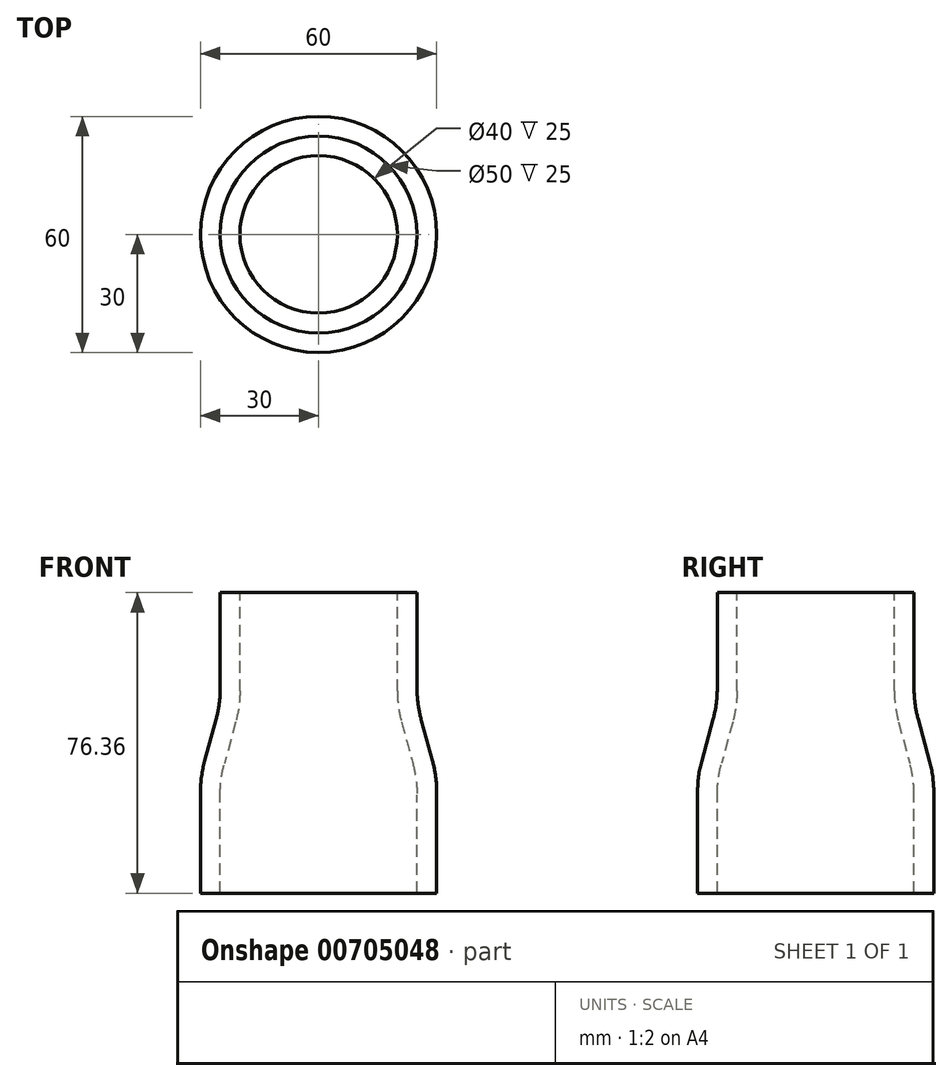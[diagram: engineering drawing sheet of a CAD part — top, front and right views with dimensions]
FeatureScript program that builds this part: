
annotation { "Feature Type Name" : "Feature", "Feature Type Description" : "" }
export const myFeature = defineFeature(function(context is Context, id is Id, definition is map)
    precondition{}
    {
        {
            var Q0;
            Q0=qCreatedBy(makeId("Front.planeOp"),FACE);
            var sketch = newSketch(context, id + "F0", { "sketchPlane" : qUnion([Q0])});
            skLineSegment(sketch, "E0", {"start": v(0, 61.45) * mm, "end": v(0, -56.79) * mm, "construction": true});
            skLineSegment(sketch, "E1", {"start": v(-25, 0) * mm, "end": v(-25, 25) * mm});
            skLineSegment(sketch, "E2", {"start": v(-23.94, 32.9) * mm, "end": v(-21.06, 43.46) * mm});
            skLineSegment(sketch, "E3", {"start": v(-20, 51.36) * mm, "end": v(-20, 76.36) * mm});
            skLineSegment(sketch, "E4.0", {"start": v(-25, 52.03) * mm, "end": v(-25, 76.36) * mm});
            skLineSegment(sketch, "E4.1", {"start": v(-28.94, 33.57) * mm, "end": v(-26.06, 44.13) * mm});
            skLineSegment(sketch, "E4.2", {"start": v(-30, 0) * mm, "end": v(-30, 25.67) * mm});
            skLineSegment(sketch, "E5", {"start": v(-25, 76.36) * mm, "end": v(-20, 76.36) * mm});
            skLineSegment(sketch, "E6", {"start": v(-30, 0) * mm, "end": v(-25, 0) * mm});
            skPoint(sketch, "E7.visualSharp", {"position": v(-25, 29.02) * mm});
            skArc(sketch, "E7.filletArc", {"start": v(-23.94, 32.9) * mm, "mid": v(-24.73, 28.99) * mm, "end": v(-25, 25) * mm});
            skPoint(sketch, "E8.visualSharp", {"position": v(-30, 29.7) * mm});
            skArc(sketch, "E8.filletArc", {"start": v(-28.94, 33.57) * mm, "mid": v(-29.73, 29.66) * mm, "end": v(-30, 25.67) * mm});
            skPoint(sketch, "E9.visualSharp", {"position": v(-20, 47.34) * mm});
            skArc(sketch, "E9.filletArc", {"start": v(-21.06, 43.46) * mm, "mid": v(-20.27, 47.37) * mm, "end": v(-20, 51.36) * mm});
            skPoint(sketch, "E10.visualSharp", {"position": v(-25, 48) * mm});
            skArc(sketch, "E10.filletArc", {"start": v(-26.06, 44.13) * mm, "mid": v(-25.27, 48.04) * mm, "end": v(-25, 52.03) * mm});
            skSolve(sketch);
        }
        {
            var Q0;
            Q0 = qSketchRegion(id + "F0", true);
            var Q1;
            Q1=sQuery(id+"F0.wireOp",EDGE,"E0");
            revolve(context, id + "F1", {"surfaceOperationType" : NewSurfaceOperationType.NEW, "entities" : qUnion([Q0]), "axis" : qUnion([Q1]), "revolveType" : RevolveType.FULL});
        }
    });
